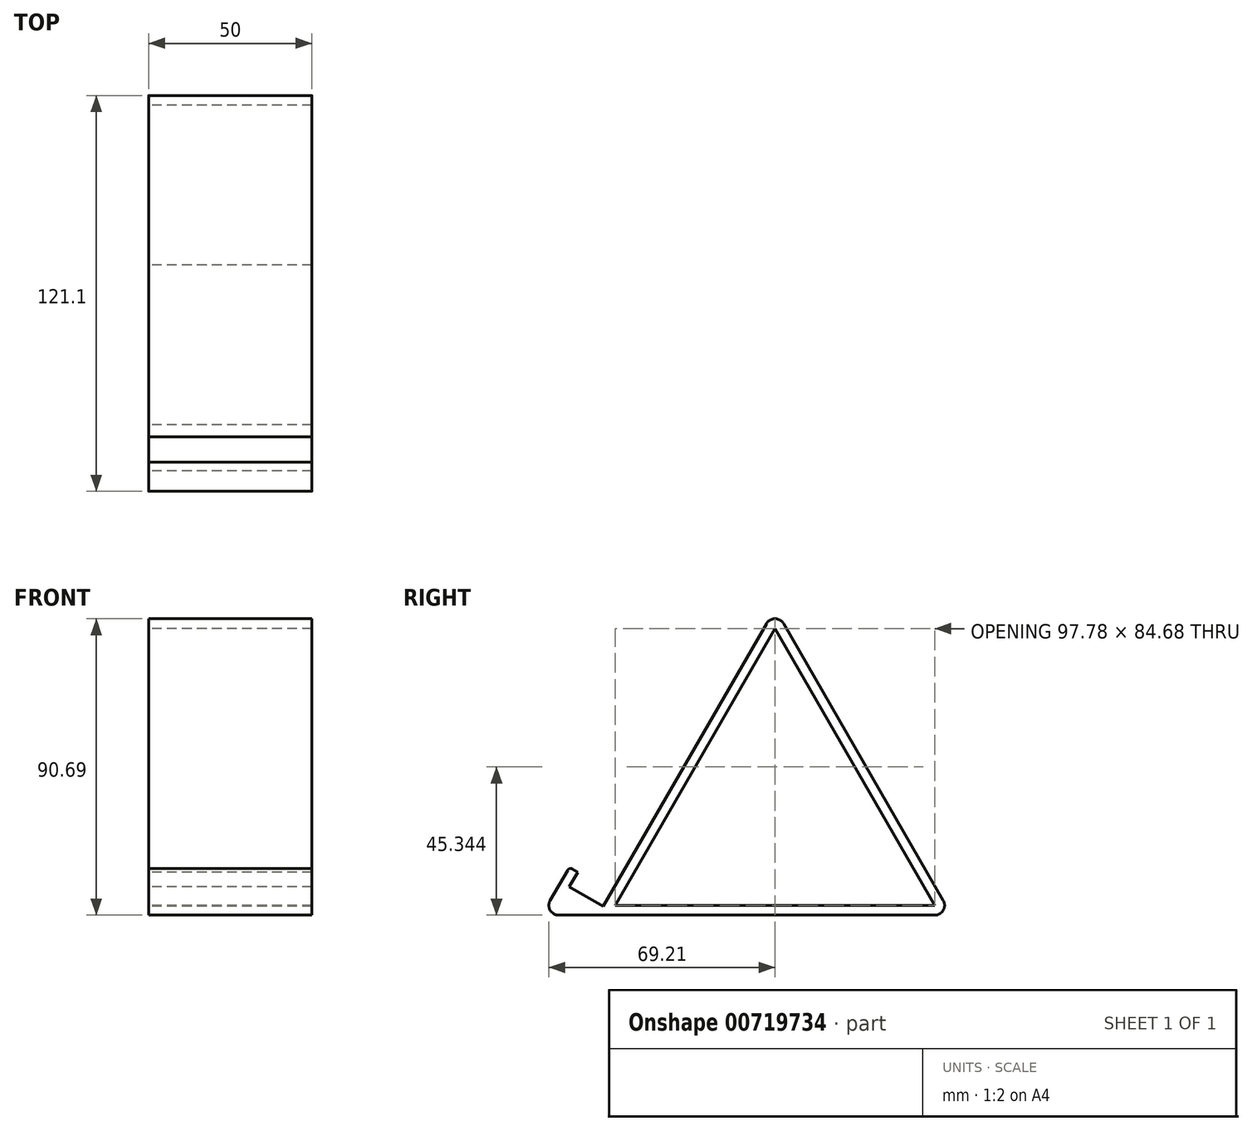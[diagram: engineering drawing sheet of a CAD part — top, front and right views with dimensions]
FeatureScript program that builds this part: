
annotation { "Feature Type Name" : "Feature", "Feature Type Description" : "" }
export const myFeature = defineFeature(function(context is Context, id is Id, definition is map)
    precondition{}
    {
        {
            var Q0;
            Q0=qCreatedBy(makeId("Right.planeOp"),FACE);
            var sketch = newSketch(context, id + "F0", { "sketchPlane" : qUnion([Q0])});
            skCircle(sketch, "E0.cCircle", {"center": v(0, 0) * mm, "radius": 31.23 * mm, "construction": true});
            skLineSegment(sketch, "E0.0", {"start": v(-54.09, -31.23) * mm, "end": v(-2.6, 57.96) * mm});
            skLineSegment(sketch, "E0.1", {"start": v(2.6, 57.96) * mm, "end": v(51.49, -26.73) * mm});
            skLineSegment(sketch, "E0.2", {"start": v(48.9, -31.23) * mm, "end": v(-54.09, -31.23) * mm});
            skPoint(sketch, "E0.0.midPoint", {"position": v(-27.04, 15.61) * mm});
            skPoint(sketch, "E1.visualSharp", {"position": v(0, 62.46) * mm});
            skArc(sketch, "E1.filletArc", {"start": v(2.6, 57.96) * mm, "mid": v(0, 59.46) * mm, "end": v(-2.6, 57.96) * mm});
            skPoint(sketch, "E2.visualSharp", {"position": v(54.09, -31.23) * mm});
            skArc(sketch, "E2.filletArc", {"start": v(48.9, -31.23) * mm, "mid": v(51.49, -29.73) * mm, "end": v(51.49, -26.73) * mm});
            skSolve(sketch);
        }
        {
            var Q0;
            Q0=makeQuery(id+"F0.imprint","IMPRINT",FACE,{"disambiguationData":[TD([[makeQuery(id+"F0.imprint","IMPRINT",EDGE,{"derivedFrom":sQuery(id+"F0.wireOp",EDGE,"E0.0")}),-1.0]])]});
            extrude(context, id + "F1", {"entities" : qUnion([Q0]), "depth" : 50 * mm, "offsetDistance" : 25 * mm});
        }
        {
            var Q0;
            Q0=makeQuery(id+"F1.opExtrude","CAP_FACE",FACE,{"disambiguationData":[OSD([sQuery(id+"F0.wireOp",EDGE,"E0.0"),sQuery(id+"F0.wireOp",EDGE,"E0.1"),sQuery(id+"F0.wireOp",EDGE,"E0.2"),sQuery(id+"F0.wireOp",EDGE,"E1.filletArc"),sQuery(id+"F0.wireOp",EDGE,"E2.filletArc")])],"isStart":false});
            var Q1;
            Q1=makeQuery(id+"F1.opExtrude","CAP_FACE",FACE,{"disambiguationData":[OSD([sQuery(id+"F0.wireOp",EDGE,"E0.0"),sQuery(id+"F0.wireOp",EDGE,"E0.1"),sQuery(id+"F0.wireOp",EDGE,"E0.2"),sQuery(id+"F0.wireOp",EDGE,"E1.filletArc"),sQuery(id+"F0.wireOp",EDGE,"E2.filletArc")])],"isStart":true});
            shell(context, id + "F2", {"entities" : qUnion([Q0, Q1]), "thickness" : 3 * mm});
        }
        {
            var Q0;
            Q0=qCreatedBy(makeId("Right.planeOp"),FACE);
            var sketch = newSketch(context, id + "F3", { "sketchPlane" : qUnion([Q0])});
            skPoint(sketch, "E3.0", {"position": v(-54.09, -31.23) * mm});
            skLineSegment(sketch, "E4.0", {"start": v(48.9, -31.23) * mm, "end": v(-54.09, -31.23) * mm});
            skLineSegment(sketch, "E5.0.0", {"start": v(-2.6, 57.96) * mm, "end": v(-54.09, -31.23) * mm});
            skLineSegment(sketch, "E5.0.2", {"start": v(-54.09, -31.23) * mm, "end": v(-2.6, 57.96) * mm});
            skLineSegment(sketch, "E6", {"start": v(-54.09, -31.23) * mm, "end": v(-66.21, -31.23) * mm});
            skLineSegment(sketch, "E7", {"start": v(-68.81, -26.73) * mm, "end": v(-63.44, -17.42) * mm});
            skLineSegment(sketch, "E8", {"start": v(-62.07, -17.06) * mm, "end": v(-60.34, -18.06) * mm});
            skLineSegment(sketch, "E9", {"start": v(-60.34, -18.06) * mm, "end": v(-62.94, -22.56) * mm});
            skLineSegment(sketch, "E10", {"start": v(-62.94, -22.56) * mm, "end": v(-52.55, -28.56) * mm});
            skPoint(sketch, "E11.visualSharp", {"position": v(-71.4, -31.23) * mm});
            skArc(sketch, "E11.filletArc", {"start": v(-68.81, -26.73) * mm, "mid": v(-68.81, -29.73) * mm, "end": v(-66.21, -31.23) * mm});
            skPoint(sketch, "E12.visualSharp", {"position": v(-62.94, -16.56) * mm});
            skArc(sketch, "E12.filletArc", {"start": v(-62.07, -17.06) * mm, "mid": v(-62.83, -16.96) * mm, "end": v(-63.44, -17.42) * mm});
            skSolve(sketch);
        }
        {
            var Q0;
            {var subQ0=sQuery(id+"F3.wireOp",EDGE,"E6");Q0=makeQuery(id+"F3.imprint","IMPRINT",FACE,{"disambiguationData":[TD([[makeQuery(id+"F3.imprint","IMPRINT",EDGE,{"derivedFrom":subQ0}),-1.0]])]});}
            extrude(context, id + "F4", {"entities" : qUnion([Q0]), "operationType" : NewBodyOperationType.ADD, "depth" : 50 * mm, "offsetDistance" : 25 * mm});
        }
    });
